# Revit family: ScanBox Single Combo
name_source: partatom
category: Mechanical Equipment
units: mm (PartAtom-declared; Revit-internal decimal feet)

## family parameters
Always vertical = Yes
Cut with Voids When Loaded = No
OmniClass Number = 23.75.00.00
OmniClass Title = Climate Control (HVAC)
Part Type = Normal
Room Calculation Point = No
Round Connector Dimension = Use Diameter
Shared = No
Work Plane-Based = No

## types (41) — shared parameters
Manufacturer = ScanBox Thermoproducts AB
TapSlam Lock = No
Top Frame Start = 170 mm  [stored 0.557743 ft]
URL = www.ScanBox.se

## per-type parameters (varying)
- Ergo Line HF 08: Assembly Code=ELSHF08; Box Depth=627 mm  [stored 2.05709 ft]; Box Height=795 mm; Box Width=420 mm  [stored 1.37795 ft]; Central Stop Pedal=Yes; Chassi Depth=810 mm; Chassi Height=193 mm; Chassi Width=540 mm; Cooler 2 Compressor=No; Cooler Compressor=No; Cooler Pelt 150=No; Cooler Pelt 200=No; Description=Ergo Line - Single - Heating Fan; Display Profile=Yes; Door Combo=No; Door Height=790 mm; Door Single=Yes; Door Upper Height=400 mm  [stored 1.31234 ft]; Excenter Lock Upper=No; FL Amps=3 A; Heater Combo=No; Heater Single=Yes; Innerframe Start=70 mm  [stored 0.229659 ft]; Model=Single; Pedal Width=125 mm  [stored 0.410105 ft]; Regulator 2=No; Rim=130 mm; TapSlam Height=248 mm; TapSlam Upper Height=200 mm  [stored 0.656168 ft]; Top Frame Bracket Start=170 mm  [stored 0.557743 ft]; Top Frame Displ=Yes; Top Frame Neutral=No; Total Height=1127 mm; Volts=230 V; Wheel Size=160 mm  [stored 0.524934 ft]
- Ergo Line HF 10: Assembly Code=ELSHF10; Box Depth=627 mm  [stored 2.05709 ft]; Box Height=955 mm; Box Width=420 mm  [stored 1.37795 ft]; Central Stop Pedal=Yes; Chassi Depth=810 mm; Chassi Height=193 mm; Chassi Width=540 mm; Cooler 2 Compressor=No; Cooler Compressor=No; Cooler Pelt 150=No; Cooler Pelt 200=No; Description=Ergo Line - Single - Heating Fan; Display Profile=Yes; Door Combo=No; Door Height=950 mm; Door Single=Yes; Door Upper Height=400 mm  [stored 1.31234 ft]; Excenter Lock Upper=No; FL Amps=3 A; Heater Combo=No; Heater Single=Yes; Innerframe Start=70 mm  [stored 0.229659 ft]; Model=Single; Pedal Width=125 mm  [stored 0.410105 ft]; Regulator 2=No; Rim=130 mm; TapSlam Height=328 mm; TapSlam Upper Height=200 mm  [stored 0.656168 ft]; Top Frame Bracket Start=170 mm  [stored 0.557743 ft]; Top Frame Displ=Yes; Top Frame Neutral=No; Total Height=1287 mm; Volts=230 V; Wheel Size=160 mm  [stored 0.524934 ft]
- Ergo Line HF 12: Assembly Code=ELSHF12; Box Depth=627 mm  [stored 2.05709 ft]; Box Height=1115 mm; Box Width=420 mm  [stored 1.37795 ft]; Central Stop Pedal=Yes; Chassi Depth=810 mm; Chassi Height=193 mm; Chassi Width=540 mm; Cooler 2 Compressor=No; Cooler Compressor=No; Cooler Pelt 150=No; Cooler Pelt 200=No; Description=Ergo Line - Single - Heating Fan; Display Profile=Yes; Door Combo=No; Door Height=1110 mm; Door Single=Yes; Door Upper Height=400 mm  [stored 1.31234 ft]; Excenter Lock Upper=No; FL Amps=5 A; Heater Combo=No; Heater Single=Yes; Innerframe Start=70 mm  [stored 0.229659 ft]; Model=Single; Pedal Width=125 mm  [stored 0.410105 ft]; Regulator 2=No; Rim=130 mm; TapSlam Height=320 mm  [stored 1.04987 ft]; TapSlam Upper Height=200 mm  [stored 0.656168 ft]; Top Frame Bracket Start=170 mm  [stored 0.557743 ft]; Top Frame Displ=Yes; Top Frame Neutral=No; Total Height=1447 mm; Volts=230 V; Wheel Size=160 mm  [stored 0.524934 ft]
- Ergo Line HF 14: Assembly Code=ELSHF14; Box Depth=627 mm  [stored 2.05709 ft]; Box Height=1275 mm; Box Width=420 mm  [stored 1.37795 ft]; Central Stop Pedal=Yes; Chassi Depth=810 mm; Chassi Height=193 mm; Chassi Width=540 mm; Cooler 2 Compressor=No; Cooler Compressor=No; Cooler Pelt 150=No; Cooler Pelt 200=No; Description=Ergo Line - Single - Heating Fan; Display Profile=Yes; Door Combo=No; Door Height=1270 mm; Door Single=Yes; Door Upper Height=400 mm  [stored 1.31234 ft]; Excenter Lock Upper=No; FL Amps=5 A; Heater Combo=No; Heater Single=Yes; Innerframe Start=70 mm  [stored 0.229659 ft]; Model=Single; Pedal Width=125 mm  [stored 0.410105 ft]; Regulator 2=No; Rim=130 mm; TapSlam Height=480 mm; TapSlam Upper Height=200 mm  [stored 0.656168 ft]; Top Frame Bracket Start=170 mm  [stored 0.557743 ft]; Top Frame Displ=Yes; Top Frame Neutral=No; Total Height=1607 mm; Volts=230 V; Wheel Size=160 mm  [stored 0.524934 ft]
- Ergo Line NE 08: Assembly Code=ELSNE08; Box Depth=627 mm  [stored 2.05709 ft]; Box Height=795 mm; Box Width=420 mm  [stored 1.37795 ft]; Central Stop Pedal=Yes; Chassi Depth=810 mm; Chassi Height=193 mm; Chassi Width=540 mm; Cooler 2 Compressor=No; Cooler Compressor=No; Cooler Pelt 150=No; Cooler Pelt 200=No; Description=Ergo Line - Single - Neutral; Display Profile=No; Door Combo=No; Door Height=790 mm; Door Single=Yes; Door Upper Height=400 mm  [stored 1.31234 ft]; Excenter Lock Upper=No; FL Amps=0 A; Heater Combo=No; Heater Single=No; Innerframe Start=70 mm  [stored 0.229659 ft]; Model=Single; Pedal Width=125 mm  [stored 0.410105 ft]; Regulator 2=No; Rim=130 mm; TapSlam Height=248 mm; TapSlam Upper Height=200 mm  [stored 0.656168 ft]; Top Frame Bracket Start=10 mm  [stored 0.0328084 ft]; Top Frame Displ=No; Top Frame Neutral=Yes; Total Height=1074 mm; Volts=0 V; Wheel Size=160 mm  [stored 0.524934 ft]
- Ergo Line NE 10: Assembly Code=ELSNE10; Box Depth=627 mm  [stored 2.05709 ft]; Box Height=955 mm; Box Width=420 mm  [stored 1.37795 ft]; Central Stop Pedal=Yes; Chassi Depth=810 mm; Chassi Height=193 mm; Chassi Width=540 mm; Cooler 2 Compressor=No; Cooler Compressor=No; Cooler Pelt 150=No; Cooler Pelt 200=No; Description=Ergo Line - Single - Neutral; Display Profile=No; Door Combo=No; Door Height=950 mm; Door Single=Yes; Door Upper Height=400 mm  [stored 1.31234 ft]; Excenter Lock Upper=No; FL Amps=0 A; Heater Combo=No; Heater Single=No; Innerframe Start=70 mm  [stored 0.229659 ft]; Model=Single; Pedal Width=125 mm  [stored 0.410105 ft]; Regulator 2=No; Rim=130 mm; TapSlam Height=328 mm; TapSlam Upper Height=200 mm  [stored 0.656168 ft]; Top Frame Bracket Start=10 mm  [stored 0.0328084 ft]; Top Frame Displ=No; Top Frame Neutral=Yes; Total Height=1234 mm; Volts=0 V; Wheel Size=160 mm  [stored 0.524934 ft]
- Ergo Line NE 12: Assembly Code=ELSNE12; Box Depth=627 mm  [stored 2.05709 ft]; Box Height=1115 mm; Box Width=420 mm  [stored 1.37795 ft]; Central Stop Pedal=Yes; Chassi Depth=810 mm; Chassi Height=193 mm; Chassi Width=540 mm; Cooler 2 Compressor=No; Cooler Compressor=No; Cooler Pelt 150=No; Cooler Pelt 200=No; Description=Ergo Line - Single - Neutral; Display Profile=No; Door Combo=No; Door Height=1110 mm; Door Single=Yes; Door Upper Height=400 mm  [stored 1.31234 ft]; Excenter Lock Upper=No; FL Amps=0 A; Heater Combo=No; Heater Single=No; Innerframe Start=70 mm  [stored 0.229659 ft]; Model=Single; Pedal Width=125 mm  [stored 0.410105 ft]; Regulator 2=No; Rim=130 mm; TapSlam Height=320 mm  [stored 1.04987 ft]; TapSlam Upper Height=200 mm  [stored 0.656168 ft]; Top Frame Bracket Start=10 mm  [stored 0.0328084 ft]; Top Frame Displ=No; Top Frame Neutral=Yes; Total Height=1394 mm; Volts=0 V; Wheel Size=160 mm  [stored 0.524934 ft]
- Ergo Line NE 14: Assembly Code=ELSNE14; Box Depth=627 mm  [stored 2.05709 ft]; Box Height=1275 mm; Box Width=420 mm  [stored 1.37795 ft]; Central Stop Pedal=Yes; Chassi Depth=810 mm; Chassi Height=193 mm; Chassi Width=540 mm; Cooler 2 Compressor=No; Cooler Compressor=No; Cooler Pelt 150=No; Cooler Pelt 200=No; Description=Ergo Line - Single - Neutral; Display Profile=No; Door Combo=No; Door Height=1270 mm; Door Single=Yes; Door Upper Height=400 mm  [stored 1.31234 ft]; Excenter Lock Upper=No; FL Amps=0 A; Heater Combo=No; Heater Single=No; Innerframe Start=70 mm  [stored 0.229659 ft]; Model=Single; Pedal Width=125 mm  [stored 0.410105 ft]; Regulator 2=No; Rim=130 mm; TapSlam Height=480 mm; TapSlam Upper Height=200 mm  [stored 0.656168 ft]; Top Frame Bracket Start=10 mm  [stored 0.0328084 ft]; Top Frame Displ=No; Top Frame Neutral=Yes; Total Height=1554 mm; Volts=0 V; Wheel Size=160 mm  [stored 0.524934 ft]
- Ergo Line CP 08: Assembly Code=ELSCP08; Box Depth=627 mm  [stored 2.05709 ft]; Box Height=795 mm; Box Width=420 mm  [stored 1.37795 ft]; Central Stop Pedal=Yes; Chassi Depth=810 mm; Chassi Height=193 mm; Chassi Width=540 mm; Cooler 2 Compressor=No; Cooler Compressor=No; Cooler Pelt 150=No; Cooler Pelt 200=Yes; Description=Ergo Line - Single - Cooling Peltier; Display Profile=Yes; Door Combo=No; Door Height=790 mm; Door Single=Yes; Door Upper Height=400 mm  [stored 1.31234 ft]; Excenter Lock Upper=No; FL Amps=1 A; Heater Combo=No; Heater Single=No; Innerframe Start=70 mm  [stored 0.229659 ft]; Model=Single; Pedal Width=125 mm  [stored 0.410105 ft]; Regulator 2=No; Rim=130 mm; TapSlam Height=248 mm; TapSlam Upper Height=200 mm  [stored 0.656168 ft]; Top Frame Bracket Start=170 mm  [stored 0.557743 ft]; Top Frame Displ=Yes; Top Frame Neutral=No; Total Height=1127 mm; Volts=230 V; Wheel Size=160 mm  [stored 0.524934 ft]
- Ergo Line CP 10: Assembly Code=ELSCP10; Box Depth=627 mm  [stored 2.05709 ft]; Box Height=955 mm; Box Width=420 mm  [stored 1.37795 ft]; Central Stop Pedal=Yes; Chassi Depth=810 mm; Chassi Height=193 mm; Chassi Width=540 mm; Cooler 2 Compressor=No; Cooler Compressor=No; Cooler Pelt 150=No; Cooler Pelt 200=Yes; Description=Ergo Line - Single - Cooling Peltier; Display Profile=Yes; Door Combo=No; Door Height=950 mm; Door Single=Yes; Door Upper Height=400 mm  [stored 1.31234 ft]; Excenter Lock Upper=No; FL Amps=1 A; Heater Combo=No; Heater Single=No; Innerframe Start=70 mm  [stored 0.229659 ft]; Model=Single; Pedal Width=125 mm  [stored 0.410105 ft]; Regulator 2=No; Rim=130 mm; TapSlam Height=328 mm; TapSlam Upper Height=200 mm  [stored 0.656168 ft]; Top Frame Bracket Start=170 mm  [stored 0.557743 ft]; Top Frame Displ=Yes; Top Frame Neutral=No; Total Height=1287 mm; Volts=230 V; Wheel Size=160 mm  [stored 0.524934 ft]
- Ergo Line CP 12: Assembly Code=ELSCP12; Box Depth=627 mm  [stored 2.05709 ft]; Box Height=1115 mm; Box Width=420 mm  [stored 1.37795 ft]; Central Stop Pedal=Yes; Chassi Depth=810 mm; Chassi Height=193 mm; Chassi Width=540 mm; Cooler 2 Compressor=No; Cooler Compressor=No; Cooler Pelt 150=No; Cooler Pelt 200=Yes; Description=Ergo Line - Single - Cooling Peltier; Display Profile=Yes; Door Combo=No; Door Height=1110 mm; Door Single=Yes; Door Upper Height=400 mm  [stored 1.31234 ft]; Excenter Lock Upper=No; FL Amps=1 A; Heater Combo=No; Heater Single=No; Innerframe Start=70 mm  [stored 0.229659 ft]; Model=Single; Pedal Width=125 mm  [stored 0.410105 ft]; Regulator 2=No; Rim=130 mm; TapSlam Height=320 mm  [stored 1.04987 ft]; TapSlam Upper Height=200 mm  [stored 0.656168 ft]; Top Frame Bracket Start=170 mm  [stored 0.557743 ft]; Top Frame Displ=Yes; Top Frame Neutral=No; Total Height=1447 mm; Volts=230 V; Wheel Size=160 mm  [stored 0.524934 ft]
- Ergo Line CP 14: Assembly Code=ELSCP14; Box Depth=627 mm  [stored 2.05709 ft]; Box Height=1275 mm; Box Width=420 mm  [stored 1.37795 ft]; Central Stop Pedal=Yes; Chassi Depth=810 mm; Chassi Height=193 mm; Chassi Width=540 mm; Cooler 2 Compressor=No; Cooler Compressor=No; Cooler Pelt 150=No; Cooler Pelt 200=Yes; Description=Ergo Line - Single - Cooling Peltier; Display Profile=Yes; Door Combo=No; Door Height=1270 mm; Door Single=Yes; Door Upper Height=400 mm  [stored 1.31234 ft]; Excenter Lock Upper=No; FL Amps=1 A; Heater Combo=No; Heater Single=No; Innerframe Start=70 mm  [stored 0.229659 ft]; Model=Single; Pedal Width=125 mm  [stored 0.410105 ft]; Regulator 2=No; Rim=130 mm; TapSlam Height=480 mm; TapSlam Upper Height=200 mm  [stored 0.656168 ft]; Top Frame Bracket Start=170 mm  [stored 0.557743 ft]; Top Frame Displ=Yes; Top Frame Neutral=No; Total Height=1607 mm; Volts=230 V; Wheel Size=160 mm  [stored 0.524934 ft]
- Ergo Line CC 08: Assembly Code=ELSCC08; Box Depth=627 mm  [stored 2.05709 ft]; Box Height=795 mm; Box Width=420 mm  [stored 1.37795 ft]; Central Stop Pedal=Yes; Chassi Depth=870 mm; Chassi Height=193 mm; Chassi Width=540 mm; Cooler 2 Compressor=No; Cooler Compressor=Yes; Cooler Pelt 150=No; Cooler Pelt 200=No; Description=Ergo Line - Single - Cooling Compressor; Display Profile=Yes; Door Combo=No; Door Height=790 mm; Door Single=Yes; Door Upper Height=400 mm  [stored 1.31234 ft]; Excenter Lock Upper=No; FL Amps=1 A; Heater Combo=No; Heater Single=No; Innerframe Start=60 mm  [stored 0.19685 ft]; Model=Single; Pedal Width=125 mm  [stored 0.410105 ft]; Regulator 2=No; Rim=130 mm; TapSlam Height=248 mm; TapSlam Upper Height=200 mm  [stored 0.656168 ft]; Top Frame Bracket Start=170 mm  [stored 0.557743 ft]; Top Frame Displ=Yes; Top Frame Neutral=No; Total Height=1127 mm; Volts=230 V; Wheel Size=160 mm  [stored 0.524934 ft]
- Ergo Line CC 10: Assembly Code=ELSCC10; Box Depth=627 mm  [stored 2.05709 ft]; Box Height=955 mm; Box Width=420 mm  [stored 1.37795 ft]; Central Stop Pedal=Yes; Chassi Depth=870 mm; Chassi Height=193 mm; Chassi Width=540 mm; Cooler 2 Compressor=No; Cooler Compressor=Yes; Cooler Pelt 150=No; Cooler Pelt 200=No; Description=Ergo Line - Single - Cooling Compressor; Display Profile=Yes; Door Combo=No; Door Height=950 mm; Door Single=Yes; Door Upper Height=400 mm  [stored 1.31234 ft]; Excenter Lock Upper=No; FL Amps=1 A; Heater Combo=No; Heater Single=No; Innerframe Start=60 mm  [stored 0.19685 ft]; Model=Single; Pedal Width=125 mm  [stored 0.410105 ft]; Regulator 2=No; Rim=130 mm; TapSlam Height=328 mm; TapSlam Upper Height=200 mm  [stored 0.656168 ft]; Top Frame Bracket Start=170 mm  [stored 0.557743 ft]; Top Frame Displ=Yes; Top Frame Neutral=No; Total Height=1287 mm; Volts=230 V; Wheel Size=160 mm  [stored 0.524934 ft]
- Ergo Line CC 12: Assembly Code=ELSCC12; Box Depth=627 mm  [stored 2.05709 ft]; Box Height=1115 mm; Box Width=420 mm  [stored 1.37795 ft]; Central Stop Pedal=Yes; Chassi Depth=870 mm; Chassi Height=193 mm; Chassi Width=540 mm; Cooler 2 Compressor=No; Cooler Compressor=Yes; Cooler Pelt 150=No; Cooler Pelt 200=No; Description=Ergo Line - Single - Cooling Compressor; Display Profile=Yes; Door Combo=No; Door Height=1110 mm; Door Single=Yes; Door Upper Height=400 mm  [stored 1.31234 ft]; Excenter Lock Upper=No; FL Amps=1 A; Heater Combo=No; Heater Single=No; Innerframe Start=60 mm  [stored 0.19685 ft]; Model=Single; Pedal Width=125 mm  [stored 0.410105 ft]; Regulator 2=No; Rim=130 mm; TapSlam Height=320 mm  [stored 1.04987 ft]; TapSlam Upper Height=200 mm  [stored 0.656168 ft]; Top Frame Bracket Start=170 mm  [stored 0.557743 ft]; Top Frame Displ=Yes; Top Frame Neutral=No; Total Height=1447 mm; Volts=230 V; Wheel Size=160 mm  [stored 0.524934 ft]
- Ergo Line CC 14: Assembly Code=ELSCC14; Box Depth=627 mm  [stored 2.05709 ft]; Box Height=1275 mm; Box Width=420 mm  [stored 1.37795 ft]; Central Stop Pedal=Yes; Chassi Depth=870 mm; Chassi Height=193 mm; Chassi Width=540 mm; Cooler 2 Compressor=No; Cooler Compressor=Yes; Cooler Pelt 150=No; Cooler Pelt 200=No; Description=Ergo Line - Single - Cooling Compressor; Display Profile=Yes; Door Combo=No; Door Height=1270 mm; Door Single=Yes; Door Upper Height=400 mm  [stored 1.31234 ft]; Excenter Lock Upper=No; FL Amps=1 A; Heater Combo=No; Heater Single=No; Innerframe Start=60 mm  [stored 0.19685 ft]; Model=Single; Pedal Width=125 mm  [stored 0.410105 ft]; Regulator 2=No; Rim=130 mm; TapSlam Height=480 mm; TapSlam Upper Height=200 mm  [stored 0.656168 ft]; Top Frame Bracket Start=170 mm  [stored 0.557743 ft]; Top Frame Displ=Yes; Top Frame Neutral=No; Total Height=1607 mm; Volts=230 V; Wheel Size=160 mm  [stored 0.524934 ft]
- Banquet Line NE 12: Assembly Code=BLSNE12; Box Depth=752 mm  [stored 2.46719 ft]; Box Height=1115 mm; Box Width=625 mm  [stored 2.05052 ft]; Central Stop Pedal=Yes; Chassi Depth=910 mm; Chassi Height=193 mm; Chassi Width=740 mm  [stored 2.42782 ft]; Cooler 2 Compressor=No; Cooler Compressor=No; Cooler Pelt 150=No; Cooler Pelt 200=No; Description=Banquet Line - Single - Neutral; Display Profile=No; Door Combo=No; Door Height=1110 mm; Door Single=Yes; Door Upper Height=400 mm  [stored 1.31234 ft]; Excenter Lock Upper=No; FL Amps=0 A; Heater Combo=No; Heater Single=No; Innerframe Start=70 mm  [stored 0.229659 ft]; Model=Single; Pedal Width=250 mm; Regulator 2=No; Rim=130 mm; TapSlam Height=320 mm  [stored 1.04987 ft]; TapSlam Upper Height=200 mm  [stored 0.656168 ft]; Top Frame Bracket Start=10 mm  [stored 0.0328084 ft]; Top Frame Displ=No; Top Frame Neutral=Yes; Total Height=1394 mm; Volts=0 V; Wheel Size=160 mm  [stored 0.524934 ft]
- Banquet Line NE 16: Assembly Code=BLSNE16; Box Depth=752 mm  [stored 2.46719 ft]; Box Height=1435 mm; Box Width=625 mm  [stored 2.05052 ft]; Central Stop Pedal=Yes; Chassi Depth=910 mm; Chassi Height=193 mm; Chassi Width=740 mm  [stored 2.42782 ft]; Cooler 2 Compressor=No; Cooler Compressor=No; Cooler Pelt 150=No; Cooler Pelt 200=No; Description=Banquet Line - Single - Neutral; Display Profile=No; Door Combo=No; Door Height=1430 mm; Door Single=Yes; Door Upper Height=400 mm  [stored 1.31234 ft]; Excenter Lock Upper=No; FL Amps=0 A; Heater Combo=No; Heater Single=No; Innerframe Start=70 mm  [stored 0.229659 ft]; Model=Single; Pedal Width=250 mm; Regulator 2=No; Rim=130 mm; TapSlam Height=640 mm; TapSlam Upper Height=200 mm  [stored 0.656168 ft]; Top Frame Bracket Start=10 mm  [stored 0.0328084 ft]; Top Frame Displ=No; Top Frame Neutral=Yes; Total Height=1714 mm; Volts=0 V; Wheel Size=160 mm  [stored 0.524934 ft]
- Banquet Line HF 12: Assembly Code=BLSHF12; Box Depth=752 mm  [stored 2.46719 ft]; Box Height=1115 mm; Box Width=625 mm  [stored 2.05052 ft]; Central Stop Pedal=Yes; Chassi Depth=910 mm; Chassi Height=193 mm; Chassi Width=740 mm  [stored 2.42782 ft]; Cooler 2 Compressor=No; Cooler Compressor=No; Cooler Pelt 150=No; Cooler Pelt 200=No; Description=Banquet Line - Single - Heating Fan; Display Profile=Yes; Door Combo=No; Door Height=1110 mm; Door Single=Yes; Door Upper Height=400 mm  [stored 1.31234 ft]; Excenter Lock Upper=No; FL Amps=8 A; Heater Combo=No; Heater Single=Yes; Innerframe Start=70 mm  [stored 0.229659 ft]; Model=Single; Pedal Width=250 mm; Regulator 2=No; Rim=130 mm; TapSlam Height=320 mm  [stored 1.04987 ft]; TapSlam Upper Height=200 mm  [stored 0.656168 ft]; Top Frame Bracket Start=170 mm  [stored 0.557743 ft]; Top Frame Displ=Yes; Top Frame Neutral=No; Total Height=1447 mm; Volts=230 V; Wheel Size=160 mm  [stored 0.524934 ft]
- Banquet Line HF 16: Assembly Code=BLSHF16; Box Depth=752 mm  [stored 2.46719 ft]; Box Height=1435 mm; Box Width=625 mm  [stored 2.05052 ft]; Central Stop Pedal=Yes; Chassi Depth=910 mm; Chassi Height=193 mm; Chassi Width=740 mm  [stored 2.42782 ft]; Cooler 2 Compressor=No; Cooler Compressor=No; Cooler Pelt 150=No; Cooler Pelt 200=No; Description=Banquet Line - Single - Heating Fan; Display Profile=Yes; Door Combo=No; Door Height=1430 mm; Door Single=Yes; Door Upper Height=400 mm  [stored 1.31234 ft]; Excenter Lock Upper=No; FL Amps=8 A; Heater Combo=No; Heater Single=Yes; Innerframe Start=70 mm  [stored 0.229659 ft]; Model=Single; Pedal Width=250 mm; Regulator 2=No; Rim=130 mm; TapSlam Height=640 mm; TapSlam Upper Height=200 mm  [stored 0.656168 ft]; Top Frame Bracket Start=170 mm  [stored 0.557743 ft]; Top Frame Displ=Yes; Top Frame Neutral=No; Total Height=1767 mm; Volts=230 V; Wheel Size=160 mm  [stored 0.524934 ft]
- Banquet Line CC 12: Assembly Code=BLSCC12; Box Depth=752 mm  [stored 2.46719 ft]; Box Height=1115 mm; Box Width=625 mm  [stored 2.05052 ft]; Central Stop Pedal=Yes; Chassi Depth=990 mm; Chassi Height=193 mm; Chassi Width=740 mm  [stored 2.42782 ft]; Cooler 2 Compressor=Yes; Cooler Compressor=No; Cooler Pelt 150=No; Cooler Pelt 200=No; Description=Banquet Line - Single - Cooling Compressor; Display Profile=Yes; Door Combo=No; Door Height=1110 mm; Door Single=Yes; Door Upper Height=400 mm  [stored 1.31234 ft]; Excenter Lock Upper=No; FL Amps=2 A; Heater Combo=No; Heater Single=No; Innerframe Start=60 mm  [stored 0.19685 ft]; Model=Single; Pedal Width=250 mm; Regulator 2=No; Rim=130 mm; TapSlam Height=320 mm  [stored 1.04987 ft]; TapSlam Upper Height=200 mm  [stored 0.656168 ft]; Top Frame Bracket Start=170 mm  [stored 0.557743 ft]; Top Frame Displ=Yes; Top Frame Neutral=No; Total Height=1447 mm; Volts=230 V; Wheel Size=160 mm  [stored 0.524934 ft]
- Banquet Line CC 16: Assembly Code=BLSCC16; Box Depth=752 mm  [stored 2.46719 ft]; Box Height=1435 mm; Box Width=625 mm  [stored 2.05052 ft]; Central Stop Pedal=Yes; Chassi Depth=990 mm; Chassi Height=193 mm; Chassi Width=740 mm  [stored 2.42782 ft]; Cooler 2 Compressor=Yes; Cooler Compressor=No; Cooler Pelt 150=No; Cooler Pelt 200=No; Description=Banquet Line - Single - Cooling Compressor; Display Profile=Yes; Door Combo=No; Door Height=1430 mm; Door Single=Yes; Door Upper Height=400 mm  [stored 1.31234 ft]; Excenter Lock Upper=No; FL Amps=2 A; Heater Combo=No; Heater Single=No; Innerframe Start=60 mm  [stored 0.19685 ft]; Model=Single; Pedal Width=250 mm; Regulator 2=No; Rim=130 mm; TapSlam Height=640 mm; TapSlam Upper Height=200 mm  [stored 0.656168 ft]; Top Frame Bracket Start=170 mm  [stored 0.557743 ft]; Top Frame Displ=Yes; Top Frame Neutral=No; Total Height=1767 mm; Volts=230 V; Wheel Size=160 mm  [stored 0.524934 ft]
- Banquet Line Combo HF06 + HF06: Assembly Code=BLCFF66; Box Depth=752 mm  [stored 2.46719 ft]; Box Height=1275 mm; Box Width=625 mm  [stored 2.05052 ft]; Central Stop Pedal=Yes; Chassi Depth=910 mm; Chassi Height=193 mm; Chassi Width=740 mm  [stored 2.42782 ft]; Cooler 2 Compressor=No; Cooler Compressor=No; Cooler Pelt 150=No; Cooler Pelt 200=No; Description=Banquet Line - Combo - Heating Fan - Heating Fan; Display Profile=Yes; Door Combo=Yes; Door Height=630 mm; Door Single=No; Door Upper Height=630 mm; Excenter Lock Upper=Yes; FL Amps=8 A; Heater Combo=Yes; Heater Single=Yes; Innerframe Start=70 mm  [stored 0.229659 ft]; Model=Combo; Pedal Width=250 mm; Regulator 2=Yes; Rim=130 mm; TapSlam Height=315 mm; TapSlam Upper Height=315 mm; Top Frame Bracket Start=170 mm  [stored 0.557743 ft]; Top Frame Displ=Yes; Top Frame Neutral=No; Total Height=1607 mm; Volts=230 V; Wheel Size=160 mm  [stored 0.524934 ft]
- Banquet Line Combo CC06 + HF06: Assembly Code=BLCCF66; Box Depth=752 mm  [stored 2.46719 ft]; Box Height=1275 mm; Box Width=625 mm  [stored 2.05052 ft]; Central Stop Pedal=Yes; Chassi Depth=990 mm; Chassi Height=193 mm; Chassi Width=740 mm  [stored 2.42782 ft]; Cooler 2 Compressor=No; Cooler Compressor=Yes; Cooler Pelt 150=No; Cooler Pelt 200=No; Description=Banquet Line - Combo - Cooling Compressor - Heating Fan; Display Profile=Yes; Door Combo=Yes; Door Height=630 mm; Door Single=No; Door Upper Height=630 mm; Excenter Lock Upper=Yes; FL Amps=5 A; Heater Combo=No; Heater Single=Yes; Innerframe Start=60 mm  [stored 0.19685 ft]; Model=Combo; Pedal Width=250 mm; Regulator 2=Yes; Rim=130 mm; TapSlam Height=315 mm; TapSlam Upper Height=315 mm; Top Frame Bracket Start=170 mm  [stored 0.557743 ft]; Top Frame Displ=Yes; Top Frame Neutral=No; Total Height=1607 mm; Volts=230 V; Wheel Size=160 mm  [stored 0.524934 ft]
- Ergo Line Combo HF06 + HF06: Assembly Code=ELCFF66; Box Depth=627 mm  [stored 2.05709 ft]; Box Height=1275 mm; Box Width=420 mm  [stored 1.37795 ft]; Central Stop Pedal=Yes; Chassi Depth=810 mm; Chassi Height=193 mm; Chassi Width=540 mm; Cooler 2 Compressor=No; Cooler Compressor=No; Cooler Pelt 150=No; Cooler Pelt 200=No; Description=Ergo Line - Combo - Heating Fan - Heating Fan; Display Profile=Yes; Door Combo=Yes; Door Height=630 mm; Door Single=No; Door Upper Height=630 mm; Excenter Lock Upper=Yes; FL Amps=4 A; Heater Combo=Yes; Heater Single=Yes; Innerframe Start=70 mm  [stored 0.229659 ft]; Model=Combo; Pedal Width=125 mm  [stored 0.410105 ft]; Regulator 2=Yes; Rim=130 mm; TapSlam Height=315 mm; TapSlam Upper Height=315 mm; Top Frame Bracket Start=170 mm  [stored 0.557743 ft]; Top Frame Displ=Yes; Top Frame Neutral=No; Total Height=1607 mm; Volts=230 V; Wheel Size=160 mm  [stored 0.524934 ft]
- Ergo Line Combo NE06 + NE06: Assembly Code=ELCNN66; Box Depth=627 mm  [stored 2.05709 ft]; Box Height=1275 mm; Box Width=420 mm  [stored 1.37795 ft]; Central Stop Pedal=Yes; Chassi Depth=810 mm; Chassi Height=193 mm; Chassi Width=540 mm; Cooler 2 Compressor=No; Cooler Compressor=No; Cooler Pelt 150=No; Cooler Pelt 200=No; Description=Ergo Line - Combo - Neutral - Neutral; Display Profile=No; Door Combo=Yes; Door Height=630 mm; Door Single=No; Door Upper Height=630 mm; Excenter Lock Upper=Yes; FL Amps=0 A; Heater Combo=No; Heater Single=No; Innerframe Start=70 mm  [stored 0.229659 ft]; Model=Combo; Pedal Width=125 mm  [stored 0.410105 ft]; Regulator 2=No; Rim=130 mm; TapSlam Height=315 mm; TapSlam Upper Height=315 mm; Top Frame Bracket Start=10 mm  [stored 0.0328084 ft]; Top Frame Displ=No; Top Frame Neutral=Yes; Total Height=1554 mm; Volts=0 V; Wheel Size=160 mm  [stored 0.524934 ft]
- Ergo Line Combo NE04 + HF04: Assembly Code=ELCNF44; Box Depth=627 mm  [stored 2.05709 ft]; Box Height=955 mm; Box Width=420 mm  [stored 1.37795 ft]; Central Stop Pedal=Yes; Chassi Depth=810 mm; Chassi Height=193 mm; Chassi Width=540 mm; Cooler 2 Compressor=No; Cooler Compressor=No; Cooler Pelt 150=No; Cooler Pelt 200=No; Description=Ergo Line - Combo - Neutral - Heating Fan; Display Profile=Yes; Door Combo=Yes; Door Height=470 mm; Door Single=No; Door Upper Height=470 mm; Excenter Lock Upper=Yes; FL Amps=2 A; Heater Combo=No; Heater Single=Yes; Innerframe Start=70 mm  [stored 0.229659 ft]; Model=Combo; Pedal Width=125 mm  [stored 0.410105 ft]; Regulator 2=No; Rim=130 mm; TapSlam Height=235 mm; TapSlam Upper Height=235 mm; Top Frame Bracket Start=170 mm  [stored 0.557743 ft]; Top Frame Displ=Yes; Top Frame Neutral=No; Total Height=1287 mm; Volts=230 V; Wheel Size=160 mm  [stored 0.524934 ft]
- Ergo Line Combo NE04 + HF06: Assembly Code=ELCNF46; Box Depth=627 mm  [stored 2.05709 ft]; Box Height=1115 mm; Box Width=420 mm  [stored 1.37795 ft]; Central Stop Pedal=Yes; Chassi Depth=810 mm; Chassi Height=193 mm; Chassi Width=540 mm; Cooler 2 Compressor=No; Cooler Compressor=No; Cooler Pelt 150=No; Cooler Pelt 200=No; Description=Ergo Line - Combo - Neutral - Heating Fan; Display Profile=Yes; Door Combo=Yes; Door Height=470 mm; Door Single=No; Door Upper Height=630 mm; Excenter Lock Upper=Yes; FL Amps=2 A; Heater Combo=No; Heater Single=Yes; Innerframe Start=70 mm  [stored 0.229659 ft]; Model=Combo; Pedal Width=125 mm  [stored 0.410105 ft]; Regulator 2=No; Rim=130 mm; TapSlam Height=235 mm; TapSlam Upper Height=315 mm; Top Frame Bracket Start=170 mm  [stored 0.557743 ft]; Top Frame Displ=Yes; Top Frame Neutral=No; Total Height=1447 mm; Volts=230 V; Wheel Size=160 mm  [stored 0.524934 ft]
- Ergo Line Combo NE04 + HF08: Assembly Code=ELCNF48; Box Depth=627 mm  [stored 2.05709 ft]; Box Height=1275 mm; Box Width=420 mm  [stored 1.37795 ft]; Central Stop Pedal=Yes; Chassi Depth=810 mm; Chassi Height=193 mm; Chassi Width=540 mm; Cooler 2 Compressor=No; Cooler Compressor=No; Cooler Pelt 150=No; Cooler Pelt 200=No; Description=Ergo Line - Combo - Neutral - Heating Fan; Display Profile=Yes; Door Combo=Yes; Door Height=470 mm; Door Single=No; Door Upper Height=790 mm; Excenter Lock Upper=Yes; FL Amps=3 A; Heater Combo=No; Heater Single=Yes; Innerframe Start=70 mm  [stored 0.229659 ft]; Model=Combo; Pedal Width=125 mm  [stored 0.410105 ft]; Regulator 2=No; Rim=130 mm; TapSlam Height=235 mm; TapSlam Upper Height=248 mm; Top Frame Bracket Start=170 mm  [stored 0.557743 ft]; Top Frame Displ=Yes; Top Frame Neutral=No; Total Height=1607 mm; Volts=230 V; Wheel Size=160 mm  [stored 0.524934 ft]
- Ergo Line Combo NE06 + HF06: Assembly Code=ELCNF66; Box Depth=627 mm  [stored 2.05709 ft]; Box Height=1275 mm; Box Width=420 mm  [stored 1.37795 ft]; Central Stop Pedal=Yes; Chassi Depth=810 mm; Chassi Height=193 mm; Chassi Width=540 mm; Cooler 2 Compressor=No; Cooler Compressor=No; Cooler Pelt 150=No; Cooler Pelt 200=No; Description=Ergo Line - Combo - Neutral - Heating Fan; Display Profile=Yes; Door Combo=Yes; Door Height=630 mm; Door Single=No; Door Upper Height=630 mm; Excenter Lock Upper=Yes; FL Amps=2 A; Heater Combo=No; Heater Single=Yes; Innerframe Start=70 mm  [stored 0.229659 ft]; Model=Combo; Pedal Width=125 mm  [stored 0.410105 ft]; Regulator 2=No; Rim=130 mm; TapSlam Height=315 mm; TapSlam Upper Height=315 mm; Top Frame Bracket Start=170 mm  [stored 0.557743 ft]; Top Frame Displ=Yes; Top Frame Neutral=No; Total Height=1607 mm; Volts=230 V; Wheel Size=160 mm  [stored 0.524934 ft]
- Ergo Line Combo CP04 + HF04: Assembly Code=ELCPF44; Box Depth=627 mm  [stored 2.05709 ft]; Box Height=955 mm; Box Width=420 mm  [stored 1.37795 ft]; Central Stop Pedal=Yes; Chassi Depth=810 mm; Chassi Height=193 mm; Chassi Width=540 mm; Cooler 2 Compressor=No; Cooler Compressor=No; Cooler Pelt 150=Yes; Cooler Pelt 200=No; Description=Ergo Line - Combo - Cooling Peltier - Heating Fan; Display Profile=Yes; Door Combo=Yes; Door Height=470 mm; Door Single=No; Door Upper Height=470 mm; Excenter Lock Upper=Yes; FL Amps=3 A; Heater Combo=No; Heater Single=Yes; Innerframe Start=70 mm  [stored 0.229659 ft]; Model=Combo; Pedal Width=125 mm  [stored 0.410105 ft]; Regulator 2=Yes; Rim=130 mm; TapSlam Height=235 mm; TapSlam Upper Height=235 mm; Top Frame Bracket Start=170 mm  [stored 0.557743 ft]; Top Frame Displ=Yes; Top Frame Neutral=No; Total Height=1287 mm; Volts=230 V; Wheel Size=160 mm  [stored 0.524934 ft]
- Ergo Line Combo CP04 + HF06: Assembly Code=ELCPF46; Box Depth=627 mm  [stored 2.05709 ft]; Box Height=1115 mm; Box Width=420 mm  [stored 1.37795 ft]; Central Stop Pedal=Yes; Chassi Depth=810 mm; Chassi Height=193 mm; Chassi Width=540 mm; Cooler 2 Compressor=No; Cooler Compressor=No; Cooler Pelt 150=Yes; Cooler Pelt 200=No; Description=Ergo Line - Combo - Cooling Peltier - Heating Fan; Display Profile=Yes; Door Combo=Yes; Door Height=470 mm; Door Single=No; Door Upper Height=630 mm; Excenter Lock Upper=Yes; FL Amps=3 A; Heater Combo=No; Heater Single=Yes; Innerframe Start=70 mm  [stored 0.229659 ft]; Model=Combo; Pedal Width=125 mm  [stored 0.410105 ft]; Regulator 2=Yes; Rim=130 mm; TapSlam Height=235 mm; TapSlam Upper Height=315 mm; Top Frame Bracket Start=170 mm  [stored 0.557743 ft]; Top Frame Displ=Yes; Top Frame Neutral=No; Total Height=1447 mm; Volts=230 V; Wheel Size=160 mm  [stored 0.524934 ft]
- Ergo Line Combo CP04 + HF08: Assembly Code=ELCPF48; Box Depth=627 mm  [stored 2.05709 ft]; Box Height=1275 mm; Box Width=420 mm  [stored 1.37795 ft]; Central Stop Pedal=Yes; Chassi Depth=810 mm; Chassi Height=193 mm; Chassi Width=540 mm; Cooler 2 Compressor=No; Cooler Compressor=No; Cooler Pelt 150=Yes; Cooler Pelt 200=No; Description=Ergo Line - Combo - Cooling Peltier - Heating Fan; Display Profile=Yes; Door Combo=Yes; Door Height=475 mm; Door Single=No; Door Upper Height=790 mm; Excenter Lock Upper=Yes; FL Amps=4 A; Heater Combo=No; Heater Single=Yes; Innerframe Start=70 mm  [stored 0.229659 ft]; Model=Combo; Pedal Width=125 mm  [stored 0.410105 ft]; Regulator 2=Yes; Rim=130 mm; TapSlam Height=235 mm; TapSlam Upper Height=248 mm; Top Frame Bracket Start=170 mm  [stored 0.557743 ft]; Top Frame Displ=Yes; Top Frame Neutral=No; Total Height=1607 mm; Volts=230 V; Wheel Size=160 mm  [stored 0.524934 ft]
- Ergo Line Combo CP06 + HF06: Assembly Code=ELCPF66; Box Depth=627 mm  [stored 2.05709 ft]; Box Height=1275 mm; Box Width=420 mm  [stored 1.37795 ft]; Central Stop Pedal=Yes; Chassi Depth=810 mm; Chassi Height=193 mm; Chassi Width=540 mm; Cooler 2 Compressor=No; Cooler Compressor=No; Cooler Pelt 150=Yes; Cooler Pelt 200=No; Description=Ergo Line - Combo - Cooling Peltier - Heating Fan; Display Profile=Yes; Door Combo=Yes; Door Height=630 mm; Door Single=No; Door Upper Height=630 mm; Excenter Lock Upper=Yes; FL Amps=3 A; Heater Combo=No; Heater Single=Yes; Innerframe Start=70 mm  [stored 0.229659 ft]; Model=Combo; Pedal Width=125 mm  [stored 0.410105 ft]; Regulator 2=Yes; Rim=130 mm; TapSlam Height=315 mm; TapSlam Upper Height=315 mm; Top Frame Bracket Start=170 mm  [stored 0.557743 ft]; Top Frame Displ=Yes; Top Frame Neutral=No; Total Height=1607 mm; Volts=230 V; Wheel Size=160 mm  [stored 0.524934 ft]
- Ergo Line Combo CC04 + HF04: Assembly Code=ELCCF44; Box Depth=627 mm  [stored 2.05709 ft]; Box Height=955 mm; Box Width=420 mm  [stored 1.37795 ft]; Central Stop Pedal=Yes; Chassi Depth=870 mm; Chassi Height=193 mm; Chassi Width=540 mm; Cooler 2 Compressor=No; Cooler Compressor=Yes; Cooler Pelt 150=No; Cooler Pelt 200=No; Description=Ergo Line - Combo - Cooling Compressor - Heating Fan; Display Profile=Yes; Door Combo=Yes; Door Height=470 mm; Door Single=No; Door Upper Height=470 mm; Excenter Lock Upper=Yes; FL Amps=3 A; Heater Combo=No; Heater Single=Yes; Innerframe Start=60 mm  [stored 0.19685 ft]; Model=Combo; Pedal Width=125 mm  [stored 0.410105 ft]; Regulator 2=Yes; Rim=130 mm; TapSlam Height=235 mm; TapSlam Upper Height=235 mm; Top Frame Bracket Start=170 mm  [stored 0.557743 ft]; Top Frame Displ=Yes; Top Frame Neutral=No; Total Height=1287 mm; Volts=230 V; Wheel Size=160 mm  [stored 0.524934 ft]
- Ergo Line Combo CC04 + HF06: Assembly Code=ELCCF46; Box Depth=627 mm  [stored 2.05709 ft]; Box Height=1115 mm; Box Width=420 mm  [stored 1.37795 ft]; Central Stop Pedal=Yes; Chassi Depth=870 mm; Chassi Height=193 mm; Chassi Width=540 mm; Cooler 2 Compressor=No; Cooler Compressor=Yes; Cooler Pelt 150=No; Cooler Pelt 200=No; Description=Ergo Line - Combo - Cooling Compressor - Heating Fan; Display Profile=Yes; Door Combo=Yes; Door Height=470 mm; Door Single=No; Door Upper Height=630 mm; Excenter Lock Upper=Yes; FL Amps=4 A; Heater Combo=No; Heater Single=Yes; Innerframe Start=60 mm  [stored 0.19685 ft]; Model=Combo; Pedal Width=125 mm  [stored 0.410105 ft]; Regulator 2=Yes; Rim=130 mm; TapSlam Height=235 mm; TapSlam Upper Height=315 mm; Top Frame Bracket Start=170 mm  [stored 0.557743 ft]; Top Frame Displ=Yes; Top Frame Neutral=No; Total Height=1447 mm; Volts=230 V; Wheel Size=160 mm  [stored 0.524934 ft]
- Ergo Line Combo CC04 + HF08: Assembly Code=ELCCF48; Box Depth=627 mm  [stored 2.05709 ft]; Box Height=1275 mm; Box Width=420 mm  [stored 1.37795 ft]; Central Stop Pedal=Yes; Chassi Depth=870 mm; Chassi Height=193 mm; Chassi Width=540 mm; Cooler 2 Compressor=No; Cooler Compressor=Yes; Cooler Pelt 150=No; Cooler Pelt 200=No; Description=Ergo Line - Combo - Cooling Compressor - Heating Fan; Display Profile=Yes; Door Combo=Yes; Door Height=470 mm; Door Single=No; Door Upper Height=790 mm; Excenter Lock Upper=Yes; FL Amps=4 A; Heater Combo=No; Heater Single=Yes; Innerframe Start=60 mm  [stored 0.19685 ft]; Model=Combo; Pedal Width=125 mm  [stored 0.410105 ft]; Regulator 2=Yes; Rim=130 mm; TapSlam Height=235 mm; TapSlam Upper Height=248 mm; Top Frame Bracket Start=170 mm  [stored 0.557743 ft]; Top Frame Displ=Yes; Top Frame Neutral=No; Total Height=1607 mm; Volts=230 V; Wheel Size=160 mm  [stored 0.524934 ft]
- Ergo Line Combo CC06 + HF06: Assembly Code=ELCCF66; Box Depth=627 mm  [stored 2.05709 ft]; Box Height=1275 mm; Box Width=420 mm  [stored 1.37795 ft]; Central Stop Pedal=Yes; Chassi Depth=870 mm; Chassi Height=193 mm; Chassi Width=540 mm; Cooler 2 Compressor=No; Cooler Compressor=Yes; Cooler Pelt 150=No; Cooler Pelt 200=No; Description=Ergo Line - Combo - Cooling Compressor - Heating Fan; Display Profile=Yes; Door Combo=Yes; Door Height=630 mm; Door Single=No; Door Upper Height=630 mm; Excenter Lock Upper=Yes; FL Amps=3 A; Heater Combo=No; Heater Single=Yes; Innerframe Start=60 mm  [stored 0.19685 ft]; Model=Combo; Pedal Width=125 mm  [stored 0.410105 ft]; Regulator 2=Yes; Rim=130 mm; TapSlam Height=315 mm; TapSlam Upper Height=315 mm; Top Frame Bracket Start=170 mm  [stored 0.557743 ft]; Top Frame Displ=Yes; Top Frame Neutral=No; Total Height=1607 mm; Volts=230 V; Wheel Size=160 mm  [stored 0.524934 ft]
- Ergo Line Under Counter HF 05: Assembly Code=ELSUF05; Box Depth=627 mm  [stored 2.05709 ft]; Box Height=520 mm  [stored 1.70604 ft]; Box Width=420 mm  [stored 1.37795 ft]; Central Stop Pedal=No; Chassi Depth=810 mm; Chassi Height=153 mm  [stored 0.501969 ft]; Chassi Width=540 mm; Cooler 2 Compressor=No; Cooler Compressor=No; Cooler Pelt 150=No; Cooler Pelt 200=No; Description=Ergo Line - Single - Under Counter - Heating Fan; Display Profile=Yes; Door Combo=No; Door Height=515 mm  [stored 1.68963 ft]; Door Single=Yes; Door Upper Height=400 mm  [stored 1.31234 ft]; Excenter Lock Upper=No; FL Amps=2 A; Heater Combo=No; Heater Single=Yes; Innerframe Start=70 mm  [stored 0.229659 ft]; Model=Single; Pedal Width=125 mm  [stored 0.410105 ft]; Regulator 2=No; Rim=95 mm; TapSlam Height=275 mm; TapSlam Upper Height=200 mm  [stored 0.656168 ft]; Top Frame Bracket Start=170 mm  [stored 0.557743 ft]; Top Frame Displ=Yes; Top Frame Neutral=No; Total Height=812 mm  [stored 2.66404 ft]; Volts=230 V; Wheel Size=125 mm  [stored 0.410105 ft]
- Banquet Line Under Counter HF 05: Assembly Code=BLSUF05; Box Depth=752 mm  [stored 2.46719 ft]; Box Height=520 mm  [stored 1.70604 ft]; Box Width=625 mm  [stored 2.05052 ft]; Central Stop Pedal=No; Chassi Depth=910 mm; Chassi Height=153 mm  [stored 0.501969 ft]; Chassi Width=740 mm  [stored 2.42782 ft]; Cooler 2 Compressor=No; Cooler Compressor=No; Cooler Pelt 150=No; Cooler Pelt 200=No; Description=Banquet Line - Single - Under Counter - Heating Fan; Display Profile=Yes; Door Combo=No; Door Height=515 mm  [stored 1.68963 ft]; Door Single=Yes; Door Upper Height=400 mm  [stored 1.31234 ft]; Excenter Lock Upper=No; FL Amps=4 A; Heater Combo=No; Heater Single=Yes; Innerframe Start=70 mm  [stored 0.229659 ft]; Model=Single; Pedal Width=250 mm; Regulator 2=No; Rim=95 mm; TapSlam Height=275 mm; TapSlam Upper Height=200 mm  [stored 0.656168 ft]; Top Frame Bracket Start=170 mm  [stored 0.557743 ft]; Top Frame Displ=Yes; Top Frame Neutral=No; Total Height=812 mm  [stored 2.66404 ft]; Volts=230 V; Wheel Size=125 mm  [stored 0.410105 ft]
- Ergo Line Under Counter CC 05: Assembly Code=ELSUC05; Box Depth=627 mm  [stored 2.05709 ft]; Box Height=520 mm  [stored 1.70604 ft]; Box Width=420 mm  [stored 1.37795 ft]; Central Stop Pedal=No; Chassi Depth=870 mm; Chassi Height=153 mm  [stored 0.501969 ft]; Chassi Width=540 mm; Cooler 2 Compressor=No; Cooler Compressor=Yes; Cooler Pelt 150=No; Cooler Pelt 200=No; Description=Ergo Line - Single - Under Counter - Cooling Compressor; Display Profile=Yes; Door Combo=No; Door Height=515 mm  [stored 1.68963 ft]; Door Single=Yes; Door Upper Height=400 mm  [stored 1.31234 ft]; Excenter Lock Upper=No; FL Amps=1 A; Heater Combo=No; Heater Single=No; Innerframe Start=60 mm  [stored 0.19685 ft]; Model=Single; Pedal Width=125 mm  [stored 0.410105 ft]; Regulator 2=No; Rim=95 mm; TapSlam Height=275 mm; TapSlam Upper Height=200 mm  [stored 0.656168 ft]; Top Frame Bracket Start=170 mm  [stored 0.557743 ft]; Top Frame Displ=Yes; Top Frame Neutral=No; Total Height=812 mm  [stored 2.66404 ft]; Volts=230 V; Wheel Size=125 mm  [stored 0.410105 ft]

note: [stored X ft] marks values corroborated as IEEE doubles in the binary element streams (Revit-internal decimal feet)

## geometry (parser evidence)
native form markers: Sweep x7
no freeform markers — native parametric forms only
